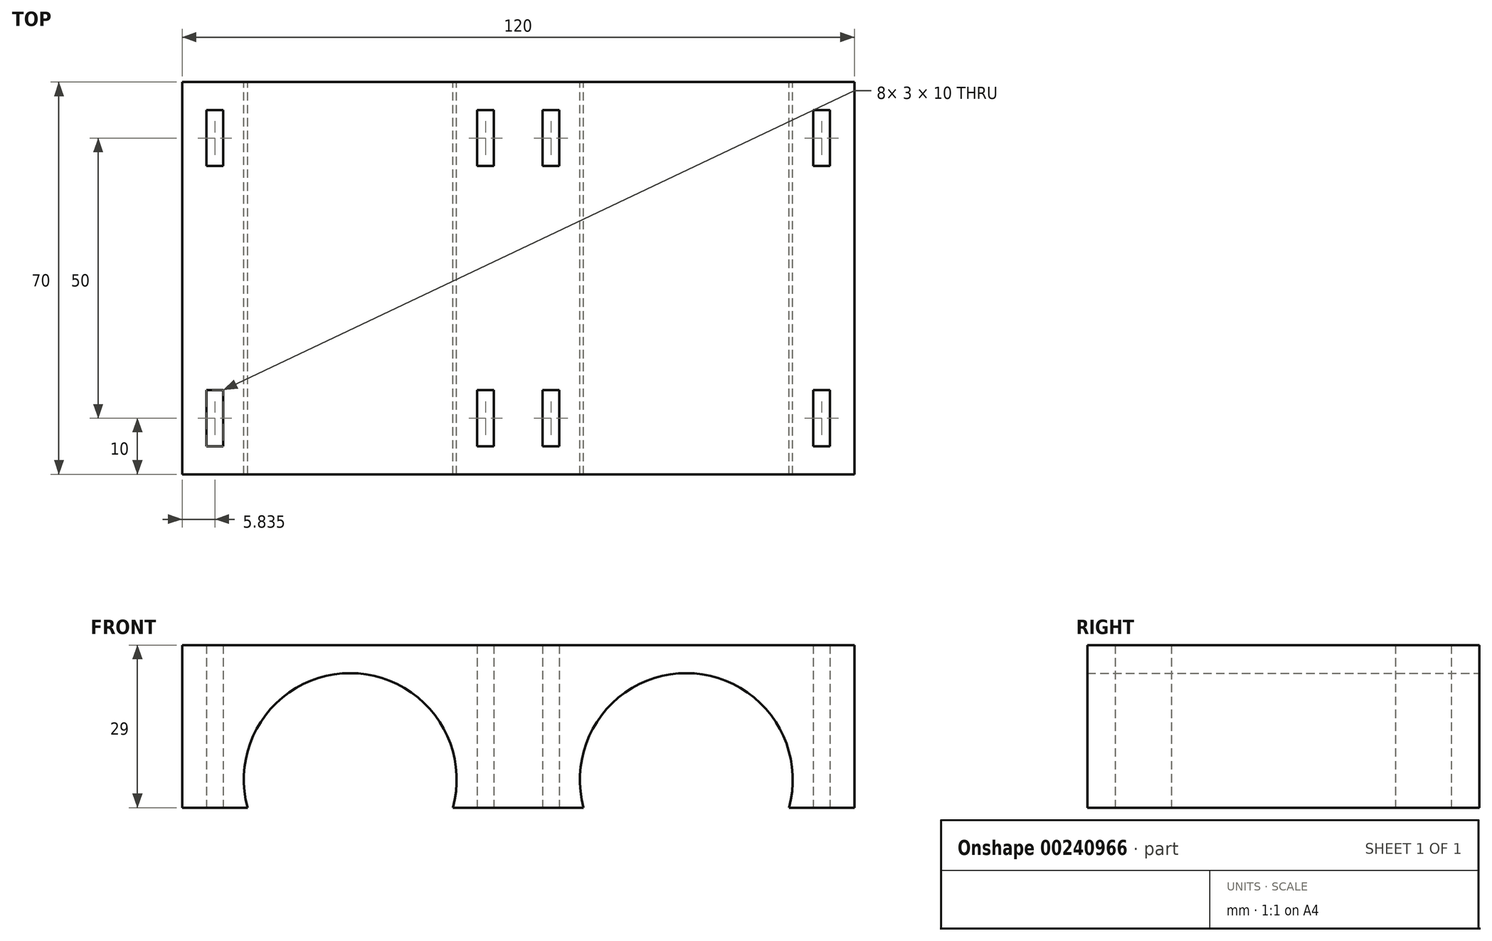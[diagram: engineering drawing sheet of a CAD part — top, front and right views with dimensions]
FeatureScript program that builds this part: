
annotation { "Feature Type Name" : "Feature", "Feature Type Description" : "" }
export const myFeature = defineFeature(function(context is Context, id is Id, definition is map)
    precondition{}
    {
        {
            var Q0;
            Q0=qCreatedBy(makeId("Front.planeOp"),FACE);
            var sketch = newSketch(context, id + "F0", { "sketchPlane" : qUnion([Q0])});
            skArc(sketch, "E0", {"start": v(-11.67, -5) * mm, "mid": v(-30, 19) * mm, "end": v(-48.33, -5) * mm});
            skLineSegment(sketch, "E1", {"start": v(-11.67, -5) * mm, "end": v(0, -5) * mm});
            skLineSegment(sketch, "E2", {"start": v(-48.33, -5) * mm, "end": v(-60, -5) * mm});
            skLineSegment(sketch, "E3", {"start": v(-60, -5) * mm, "end": v(-60, 24) * mm});
            skLineSegment(sketch, "E4", {"start": v(-60, 24) * mm, "end": v(0, 24) * mm});
            skLineSegment(sketch, "E5", {"start": v(0, 24) * mm, "end": v(0, -5) * mm, "construction": true});
            skLineSegment(sketch, "E6.MirrorCS", {"start": v(60, 24) * mm, "end": v(0, 24) * mm});
            skArc(sketch, "E7.MirrorCS", {"start": v(11.67, -5) * mm, "mid": v(30, 19) * mm, "end": v(48.33, -5) * mm});
            skLineSegment(sketch, "E8.MirrorCS", {"start": v(11.67, -5) * mm, "end": v(0, -5) * mm});
            skLineSegment(sketch, "E9.MirrorCS", {"start": v(48.33, -5) * mm, "end": v(60, -5) * mm});
            skLineSegment(sketch, "E10.MirrorCS", {"start": v(60, -5) * mm, "end": v(60, 24) * mm});
            skSolve(sketch);
        }
        {
            var Q0;
            Q0 = qSketchRegion(id + "F0", true);
            extrude(context, id + "F1", {"entities" : qUnion([Q0]), "depth" : 70 * mm});
        }
        {
            var Q0;
            Q0=makeQuery(id+"F1.opExtrude","SWEPT_FACE",FACE,{"disambiguationData":[OSD([sQuery(id+"F0.wireOp",EDGE,"E1"),sQuery(id+"F0.wireOp",EDGE,"E8.MirrorCS")])]});
            var sketch = newSketch(context, id + "F2", { "sketchPlane" : qUnion([Q0])});
            skLineSegment(sketch, "E11.bottom", {"start": v(-55.67, 65) * mm, "end": v(-52.67, 65) * mm});
            skLineSegment(sketch, "E11.top", {"start": v(-55.67, 55) * mm, "end": v(-52.67, 55) * mm});
            skLineSegment(sketch, "E11.left", {"start": v(-55.67, 65) * mm, "end": v(-55.67, 55) * mm});
            skLineSegment(sketch, "E11.right", {"start": v(-52.67, 65) * mm, "end": v(-52.67, 55) * mm});
            skLineSegment(sketch, "E12", {"start": v(0, 70) * mm, "end": v(0, 0) * mm, "construction": true});
            skLineSegment(sketch, "E13", {"start": v(0, 0) * mm, "end": v(-60, 0) * mm, "construction": true});
            skLineSegment(sketch, "E14", {"start": v(-30, 0) * mm, "end": v(-30, 35) * mm, "construction": true});
            skPoint(sketch, "E14.endSnap0", {"position": v(0, 35) * mm});
            skLineSegment(sketch, "E15.MirrorCS", {"start": v(-4.33, 65) * mm, "end": v(-7.33, 65) * mm});
            skLineSegment(sketch, "E16.MirrorCS", {"start": v(-4.33, 65) * mm, "end": v(-4.33, 55) * mm});
            skLineSegment(sketch, "E17.MirrorCS", {"start": v(-7.33, 65) * mm, "end": v(-7.33, 55) * mm});
            skLineSegment(sketch, "E18.MirrorCS", {"start": v(-4.33, 55) * mm, "end": v(-7.33, 55) * mm});
            skLineSegment(sketch, "E19", {"start": v(-30, 35) * mm, "end": v(0, 35) * mm, "construction": true});
            skLineSegment(sketch, "E20.MirrorCS", {"start": v(-4.33, 15) * mm, "end": v(-7.33, 15) * mm});
            skLineSegment(sketch, "E21.MirrorCS", {"start": v(-7.33, 5) * mm, "end": v(-7.33, 15) * mm});
            skLineSegment(sketch, "E22.MirrorCS", {"start": v(-4.33, 5) * mm, "end": v(-7.33, 5) * mm});
            skLineSegment(sketch, "E23.MirrorCS", {"start": v(-4.33, 5) * mm, "end": v(-4.33, 15) * mm});
            skLineSegment(sketch, "E24.MirrorCS", {"start": v(-52.67, 5) * mm, "end": v(-52.67, 15) * mm});
            skLineSegment(sketch, "E25.MirrorCS", {"start": v(-55.67, 5) * mm, "end": v(-52.67, 5) * mm});
            skLineSegment(sketch, "E26.MirrorCS", {"start": v(-55.67, 5) * mm, "end": v(-55.67, 15) * mm});
            skLineSegment(sketch, "E27.MirrorCS", {"start": v(-55.67, 15) * mm, "end": v(-52.67, 15) * mm});
            skLineSegment(sketch, "E28.MirrorCS", {"start": v(0, 0) * mm, "end": v(60, 0) * mm, "construction": true});
            skLineSegment(sketch, "E29.MirrorCS", {"start": v(52.67, 65) * mm, "end": v(52.67, 55) * mm});
            skLineSegment(sketch, "E30.MirrorCS", {"start": v(55.67, 65) * mm, "end": v(55.67, 55) * mm});
            skLineSegment(sketch, "E31.MirrorCS", {"start": v(55.67, 15) * mm, "end": v(52.67, 15) * mm});
            skLineSegment(sketch, "E32.MirrorCS", {"start": v(55.67, 65) * mm, "end": v(52.67, 65) * mm});
            skLineSegment(sketch, "E33.MirrorCS", {"start": v(55.67, 55) * mm, "end": v(52.67, 55) * mm});
            skLineSegment(sketch, "E34.MirrorCS", {"start": v(55.67, 5) * mm, "end": v(52.67, 5) * mm});
            skLineSegment(sketch, "E35.MirrorCS", {"start": v(55.67, 5) * mm, "end": v(55.67, 15) * mm});
            skLineSegment(sketch, "E36.MirrorCS", {"start": v(52.67, 5) * mm, "end": v(52.67, 15) * mm});
            skLineSegment(sketch, "E37.MirrorCS", {"start": v(4.33, 15) * mm, "end": v(7.33, 15) * mm});
            skLineSegment(sketch, "E38.MirrorCS", {"start": v(4.33, 5) * mm, "end": v(4.33, 15) * mm});
            skLineSegment(sketch, "E39.MirrorCS", {"start": v(4.33, 5) * mm, "end": v(7.33, 5) * mm});
            skLineSegment(sketch, "E40.MirrorCS", {"start": v(7.33, 5) * mm, "end": v(7.33, 15) * mm});
            skLineSegment(sketch, "E41.MirrorCS", {"start": v(4.33, 65) * mm, "end": v(7.33, 65) * mm});
            skLineSegment(sketch, "E42.MirrorCS", {"start": v(7.33, 65) * mm, "end": v(7.33, 55) * mm});
            skLineSegment(sketch, "E43.MirrorCS", {"start": v(4.33, 55) * mm, "end": v(7.33, 55) * mm});
            skLineSegment(sketch, "E44.MirrorCS", {"start": v(4.33, 65) * mm, "end": v(4.33, 55) * mm});
            skLineSegment(sketch, "E45", {"start": v(-60, 70) * mm, "end": v(-48.33, 70) * mm, "construction": true});
            skLineSegment(sketch, "E46", {"start": v(-54.17, 70) * mm, "end": v(-54.17, 65) * mm, "construction": true});
            skSolve(sketch);
        }
        {
            var Q0;
            Q0 = qSketchRegion(id + "F2", true);
            extrude(context, id + "F3", {"entities" : qUnion([Q0]), "operationType" : NewBodyOperationType.REMOVE, "endBound" : BoundingType.THROUGH_ALL, "oppositeDirection" : true, "depth" : 25 * mm});
        }
    });
